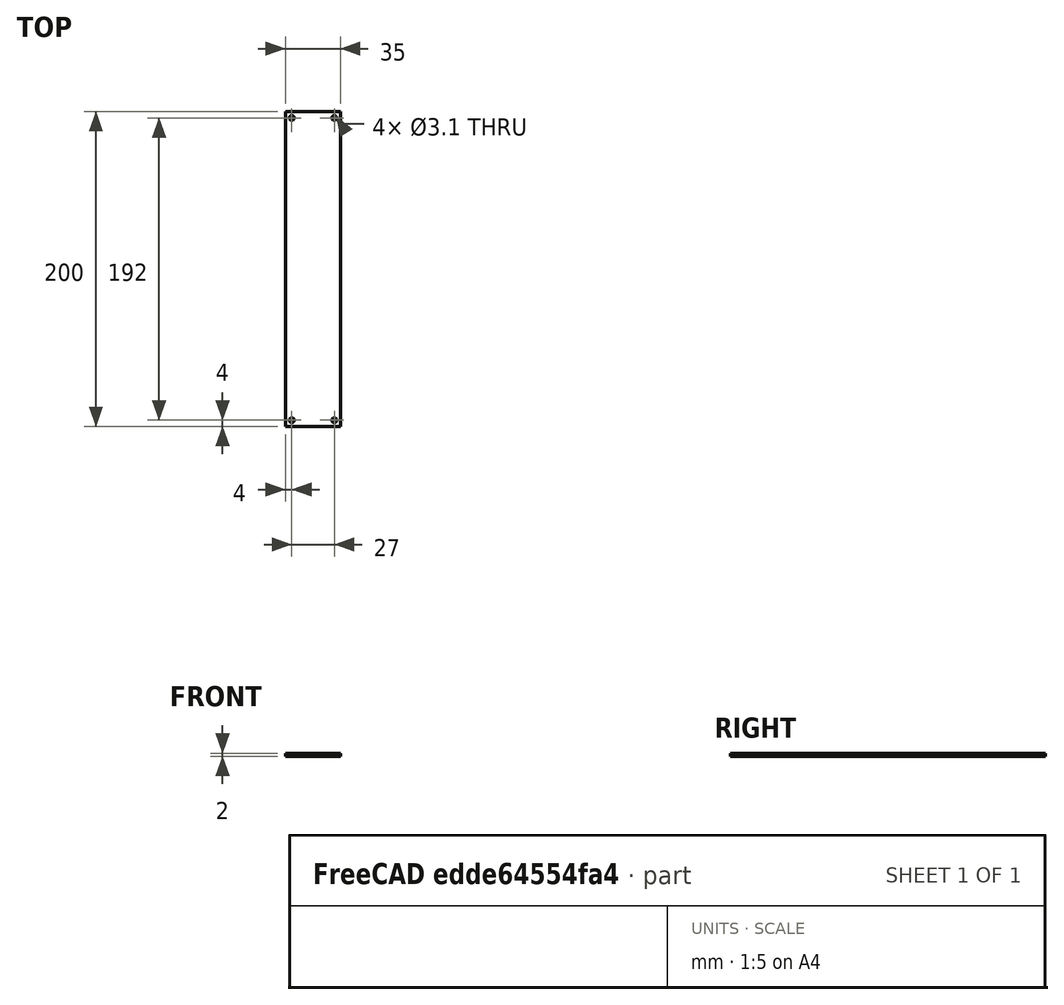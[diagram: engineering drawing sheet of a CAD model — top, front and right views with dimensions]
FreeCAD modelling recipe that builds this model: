
FCSTD DOCUMENT  (FreeCAD 0.20R29410 (Git))
Label: top_plate
License: All rights reserved
LicenseURL: http://en.wikipedia.org/wiki/All_rights_reserved
objects: PartDesign::CoordinateSystem×2, Sketcher::SketchObject×1, PartDesign::Pad×1, PartDesign::Body×1
note: 6 computed .brp shape members not serialized (recipe doc carries the construction recipe); baked Part::Feature solids carry a one-line shape summary decoded from their .brp

FEATURE [Sketcher::SketchObject] Sketch
  FullyConstrained = true
  MapMode = 5
  Support = -> [XY_Plane]
  sketch-geometry (8):
    g0: LineSegment StartX=-17.5 StartY=100 StartZ=0 EndX=17.5 EndY=100 EndZ=0
    g1: LineSegment StartX=17.5 StartY=100 StartZ=0 EndX=17.5 EndY=-100 EndZ=0
    g2: LineSegment StartX=17.5 StartY=-100 StartZ=0 EndX=-17.5 EndY=-100 EndZ=0
    g3: LineSegment StartX=-17.5 StartY=-100 StartZ=0 EndX=-17.5 EndY=100 EndZ=0
    g4: Circle CenterX=-13.5 CenterY=-96 CenterZ=0 NormalX=0 NormalY=0 NormalZ=1 AngleXU=0 Radius=1.55
    g5: Circle CenterX=13.5 CenterY=-96 CenterZ=0 NormalX=0 NormalY=0 NormalZ=1 AngleXU=0 Radius=1.55
    g6: Circle CenterX=-13.5 CenterY=96 CenterZ=0 NormalX=0 NormalY=0 NormalZ=1 AngleXU=0 Radius=1.55
    g7: Circle CenterX=13.5 CenterY=96 CenterZ=0 NormalX=0 NormalY=0 NormalZ=1 AngleXU=0 Radius=1.55
  constraints (20):
    c: Coincident(g0,g1)
    c: Coincident(g1,g2)
    c: Coincident(g2,g3)
    c: Coincident(g3,g0)
    c: Horizontal(g0)
    c: Vertical(g3)
    c: DistanceX(g2,g2) = 35
    c: Symmetric(g2,g1,g-2)
    c: Symmetric(g1,g0,g-1)
    c: DistanceY(g1,g1) = 200
    c: Symmetric(g5,g4,g-2)
    c: Equal(g4,g5)
    c: Diameter(g5) = 3.1
    c: DistanceY(g1,g5) = 4
    c: DistanceX(g5,g1) = 4
    c: Equal(g7,g6)
    c: Symmetric(g7,g6,g-2)
    c: DistanceX(g7,g0) = 4
    c: DistanceY(g7,g0) = 4
    c: Diameter(g7) = 3.1
FEATURE [PartDesign::Pad] Pad
  Direction = (0,0,1)
  Length = 2
  Length2 = 10
  Profile = -> Sketch
  ReferenceAxis = -> Sketch [N_Axis]
  Type = 0
FEATURE [PartDesign::CoordinateSystem] LCS_1
  AttacherType = Attacher::AttachEngine3D
  MapMode = 11
  Placement = pos=(-13.5,96,0) rot=(0,0,1;1.5708rad)
  Support = -> [Pad]
FEATURE [PartDesign::CoordinateSystem] LCS_2
  AttacherType = Attacher::AttachEngine3D
  MapMode = 11
  Placement = pos=(13.5,96,0) rot=(0,0,1;1.5708rad)
  Support = -> [Pad]
FEATURE [PartDesign::Body] Body
  Group = -> [Sketch,Pad,LCS_1,LCS_2]
  Origin = -> Origin
  Tip = -> Pad
